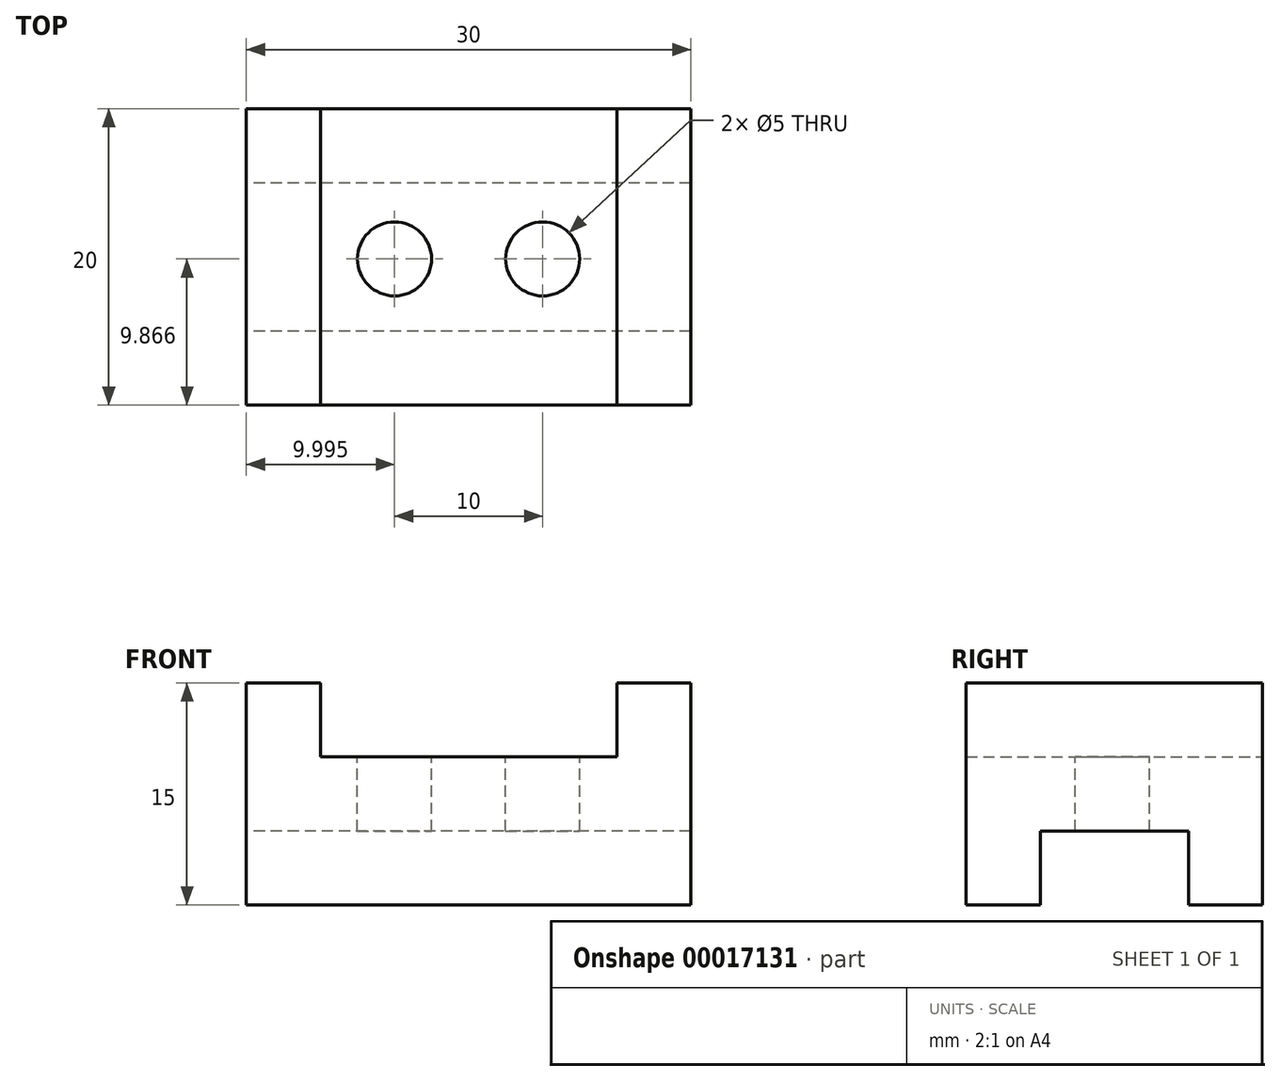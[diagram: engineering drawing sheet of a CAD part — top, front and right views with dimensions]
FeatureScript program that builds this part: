
annotation { "Feature Type Name" : "Feature", "Feature Type Description" : "" }
export const myFeature = defineFeature(function(context is Context, id is Id, definition is map)
    precondition{}
    {
        {
            var Q0;
            Q0=qCreatedBy(makeId("Front.planeOp"),FACE);
            var sketch = newSketch(context, id + "F0", { "sketchPlane" : qUnion([Q0])});
            skLineSegment(sketch, "E0", {"start": v(-13.13, 5) * mm, "end": v(-13.13, -10) * mm});
            skLineSegment(sketch, "E1", {"start": v(-13.13, -10) * mm, "end": v(16.87, -10) * mm});
            skLineSegment(sketch, "E2", {"start": v(16.87, -10) * mm, "end": v(16.87, 5) * mm});
            skLineSegment(sketch, "E3", {"start": v(-13.13, 5) * mm, "end": v(-8.13, 5) * mm});
            skLineSegment(sketch, "E4", {"start": v(-8.13, 5) * mm, "end": v(-8.13, 0) * mm});
            skLineSegment(sketch, "E5", {"start": v(16.87, 5) * mm, "end": v(11.87, 5) * mm});
            skLineSegment(sketch, "E6", {"start": v(-8.13, 0) * mm, "end": v(11.87, 0) * mm});
            skLineSegment(sketch, "E7", {"start": v(11.87, 0) * mm, "end": v(11.87, 5) * mm});
            skSolve(sketch);
        }
        {
            var Q0;
            Q0=makeQuery(id+"F0.imprint","IMPRINT",FACE,{"disambiguationData":[TD([[makeQuery(id+"F0.imprint","IMPRINT",EDGE,{"derivedFrom":sQuery(id+"F0.wireOp",EDGE,"E0")}),1.0]])]});
            extrude(context, id + "F1", {"entities" : qUnion([Q0]), "depth" : 20 * mm});
        }
        {
            var Q0;
            Q0=makeQuery(id+"F1.opExtrude","SWEPT_FACE",FACE,{"disambiguationData":[OSD([sQuery(id+"F0.wireOp",EDGE,"E0")])]});
            var sketch = newSketch(context, id + "F2", { "sketchPlane" : qUnion([Q0])});
            skLineSegment(sketch, "E8", {"start": v(5, -10) * mm, "end": v(5, -5) * mm});
            skLineSegment(sketch, "E9", {"start": v(5, -5) * mm, "end": v(15, -5) * mm});
            skLineSegment(sketch, "E10", {"start": v(15, -5) * mm, "end": v(15, -10) * mm});
            skLineSegment(sketch, "E11", {"start": v(15, -10) * mm, "end": v(20, -10) * mm});
            skLineSegment(sketch, "E12", {"start": v(5, -10) * mm, "end": v(0, -10) * mm});
            skLineSegment(sketch, "E13", {"start": v(5, -10) * mm, "end": v(15, -10) * mm});
            skSolve(sketch);
        }
        {
            var Q0;
            Q0=makeQuery(id+"F2.imprint","IMPRINT",FACE,{"disambiguationData":[TD([[makeQuery(id+"F2.imprint","IMPRINT",EDGE,{"derivedFrom":sQuery(id+"F2.wireOp",EDGE,"E8")}),-1.0]])]});
            extrude(context, id + "F3", {"entities" : qUnion([Q0]), "operationType" : NewBodyOperationType.REMOVE, "endBound" : BoundingType.THROUGH_ALL, "oppositeDirection" : true, "depth" : 25 * mm});
        }
        {
            var Q0;
            Q0=makeQuery(id+"F1.opExtrude","SWEPT_FACE",FACE,{"disambiguationData":[OSD([sQuery(id+"F0.wireOp",EDGE,"E6")])]});
            var sketch = newSketch(context, id + "F4", { "sketchPlane" : qUnion([Q0])});
            skCircle(sketch, "E14", {"center": v(-3.13, -10.13) * mm, "radius": 2.5 * mm});
            skCircle(sketch, "E15", {"center": v(6.87, -10.13) * mm, "radius": 2.5 * mm});
            skSolve(sketch);
        }
        {
            var Q0;
            Q0=makeQuery(id+"F4.imprint","IMPRINT",FACE,{"disambiguationData":[TD([[makeQuery(id+"F4.imprint","IMPRINT",EDGE,{"derivedFrom":sQuery(id+"F4.wireOp",EDGE,"E14")}),1.0]])]});
            var Q1;
            Q1=makeQuery(id+"F4.imprint","IMPRINT",FACE,{"disambiguationData":[TD([[makeQuery(id+"F4.imprint","IMPRINT",EDGE,{"derivedFrom":sQuery(id+"F4.wireOp",EDGE,"E15")}),1.0]])]});
            extrude(context, id + "F5", {"entities" : qUnion([Q0, Q1]), "operationType" : NewBodyOperationType.REMOVE, "endBound" : BoundingType.THROUGH_ALL, "oppositeDirection" : true, "depth" : 25 * mm});
        }
    });
